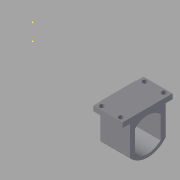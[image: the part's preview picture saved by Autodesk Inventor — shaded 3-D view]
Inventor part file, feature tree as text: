
AUTODESK INVENTOR PART (.ipt)
format: ipt  version: 2015 (Build 190159000, 159)  size: 237,568 bytes
history: native  units: in
note: dims shown in document units (in); Inventor stores cm internally (conversion verified against a paired STEP export)
features: sketch x15, extrude x13, fillet x2, plane x1, pattern_circular x1
ambient origin geometry x8: Origin, YZ Plane, XZ Plane, XY Plane, X Axis, Y Axis, Z Axis, Center Point
bodies: Solid1 (feature_tree)
feature tree (32):
  extrude  "Extrusion1"  Depth=0.1181in
  fillet  "Fillet1"  Radius=0.1969in
  fillet  "Fillet2"  [1 undecoded]
  plane  "Work Plane1"
  extrude  "Extrusion3"  Depth=0.1181in
  pattern_circular  "Circular Pattern1"  Count=4 Angle=360.0deg
  extrude  "Extrusion5"  Depth=0.1181in TaperAngle=0.0deg
  extrude  "Extrusion6"  Depth=0.1181in TaperAngle=0.0deg
  extrude  "Extrusion7"  Depth=0.3937in TaperAngle=0.0deg
  sketch  "Sketch11"  dims[d39=0.1969in d40=0.1181in d41=0.0in]
  extrude  "Extrusion8"  Depth=3.937in TaperAngle=0.0deg
  extrude  "Extrusion9"  Depth=0.1181in TaperAngle=0.0deg
  extrude  "Extrusion10"  Depth=0.5512in
  sketch  "Sketch15"  dims[d53=0.5118in d54=0.0in d55=0.5512in]
  extrude  "Extrusion11"  Depth=0.7087in
  extrude  "Extrusion12"  Depth=0.3937in
  extrude  "Extrusion13"  Depth=0.1181in TaperAngle=0.0deg
  extrude  "Extrusion14"  Depth=0.1181in
  extrude  "Extrusion15"  Depth=0.1181in TaperAngle=0.0deg
  sketch  "Sketch1"  dims[d4=0.1181in d5=0.0in d6=0.1969in d7=0.1969in d8=-0.1969in]
  sketch  "Sketch6"  dims[d17=0.7087in d21=0.1181in]
  sketch  "Sketch8"  dims[d22=0.1181in]
  sketch  "Sketch9"  dims[d24=0.7087in d25=0.0in d26=1.5748in d27=360.0deg]
  sketch  "Sketch10"  dims[d35=0.1969in d36=0.1181in d37=0.0in]
  sketch  "Sketch12"  dims[d42=0.3937in d43=0.0in d44=3.937in d45=0.0in]
  sketch  "Sketch13"  dims[d46=3.937in d47=0.0in d48=3.937in d49=0.0in]
  sketch  "Sketch14"  dims[d50=0.1181in d51=3.937in d52=0.0in]
  sketch  "Sketch17"  dims[d56=0.126in d57=0.7087in]
  sketch  "Sketch18"  dims[d58=0.3937in d59=0.3937in]
  sketch  "Sketch20"  dims[d60=0.7087in d61=0.0in d62=0.1181in d63=0.0in]
  sketch  "Sketch22"  dims[d64=0.1181in d65=0.1181in]
  sketch  "Sketch23"  dims[d66=0.1181in d67=0.1575in d68=0.0in]
note: 1 required parameter value undecoded (feature->parameter linkage not recoverable at this tier; creation-order binding heuristic only, values carry confidence <= 0.55)
